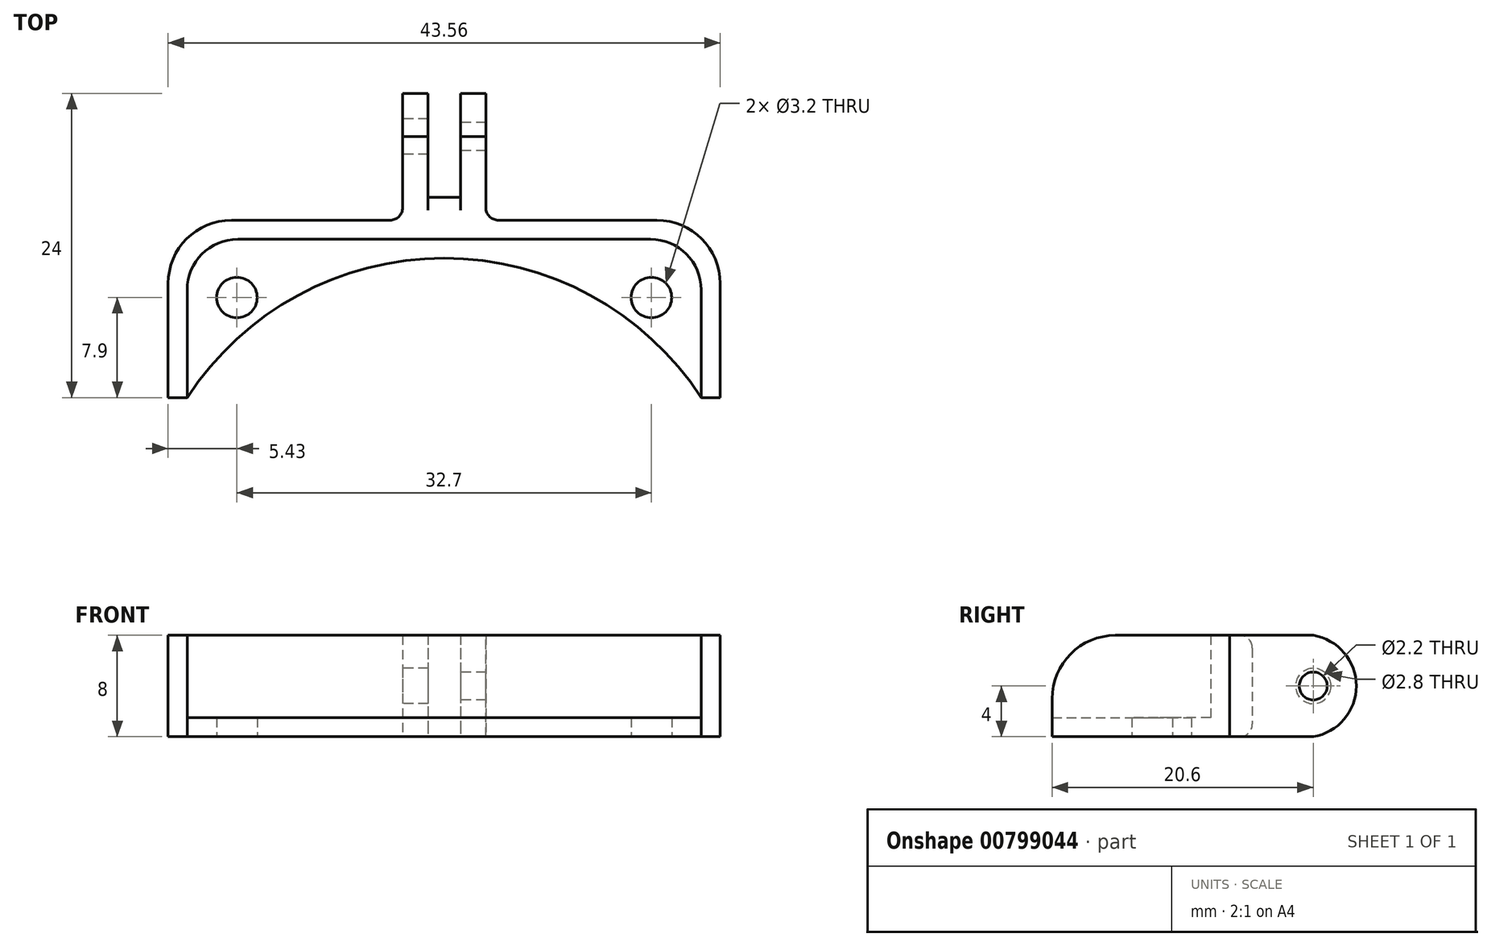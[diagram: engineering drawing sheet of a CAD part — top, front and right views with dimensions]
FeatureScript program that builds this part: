
annotation { "Feature Type Name" : "Feature", "Feature Type Description" : "" }
export const myFeature = defineFeature(function(context is Context, id is Id, definition is map)
    precondition{}
    {
        {
            var Q0;
            Q0=qCreatedBy(makeId("Top.planeOp"),FACE);
            var sketch = newSketch(context, id + "F0", { "sketchPlane" : qUnion([Q0])});
            skLineSegment(sketch, "E0", {"start": v(0, 0) * mm, "end": v(1.28, 0) * mm});
            skLineSegment(sketch, "E1", {"start": v(0, 8.06) * mm, "end": v(0, -20.77) * mm, "construction": true});
            skLineSegment(sketch, "E2", {"start": v(1.28, 0) * mm, "end": v(1.28, 8.2) * mm});
            skLineSegment(sketch, "E3", {"start": v(1.28, 8.2) * mm, "end": v(3.28, 8.2) * mm});
            skLineSegment(sketch, "E4", {"start": v(3.28, 8.2) * mm, "end": v(3.28, -1.8) * mm});
            skLineSegment(sketch, "E5", {"start": v(3.28, -1.8) * mm, "end": v(16.78, -1.8) * mm});
            skLineSegment(sketch, "E6", {"start": v(21.78, -6.8) * mm, "end": v(21.78, -15.8) * mm});
            skLineSegment(sketch, "E7", {"start": v(21.78, -15.8) * mm, "end": v(20.28, -15.8) * mm});
            skLineSegment(sketch, "E8", {"start": v(20.28, -15.8) * mm, "end": v(20.28, -7.3) * mm});
            skLineSegment(sketch, "E9", {"start": v(16.28, -3.3) * mm, "end": v(0, -3.3) * mm});
            skCircle(sketch, "E10", {"center": v(16.35, -7.9) * mm, "radius": 1.6 * mm});
            skPoint(sketch, "E11", {"position": v(0, -4.8) * mm});
            skLineSegment(sketch, "E12.MirrorCS", {"start": v(0, 0) * mm, "end": v(-1.28, 0) * mm});
            skLineSegment(sketch, "E13.MirrorCS", {"start": v(-1.28, 0) * mm, "end": v(-1.28, 8.2) * mm});
            skLineSegment(sketch, "E14.MirrorCS", {"start": v(-1.28, 8.2) * mm, "end": v(-3.28, 8.2) * mm});
            skLineSegment(sketch, "E15.MirrorCS", {"start": v(-3.28, 8.2) * mm, "end": v(-3.28, -1.8) * mm});
            skLineSegment(sketch, "E16.MirrorCS", {"start": v(-3.28, -1.8) * mm, "end": v(-16.78, -1.8) * mm});
            skLineSegment(sketch, "E17.MirrorCS", {"start": v(-21.78, -6.8) * mm, "end": v(-21.78, -15.8) * mm});
            skLineSegment(sketch, "E18.MirrorCS", {"start": v(-21.78, -15.8) * mm, "end": v(-20.28, -15.8) * mm});
            skLineSegment(sketch, "E19.MirrorCS", {"start": v(-20.28, -15.8) * mm, "end": v(-20.28, -7.3) * mm});
            skLineSegment(sketch, "E20.MirrorCS", {"start": v(-16.28, -3.3) * mm, "end": v(0, -3.3) * mm});
            skCircle(sketch, "E21.MirrorC", {"center": v(-16.35, -7.9) * mm, "radius": 1.6 * mm});
            skArc(sketch, "E22", {"start": v(20.28, -15.8) * mm, "mid": v(0, -4.8) * mm, "end": v(-20.28, -15.8) * mm});
            skPoint(sketch, "E23.visualSharp", {"position": v(20.28, -3.3) * mm});
            skArc(sketch, "E23.filletArc", {"start": v(20.28, -7.3) * mm, "mid": v(19.1, -4.47) * mm, "end": v(16.28, -3.3) * mm});
            skPoint(sketch, "E24.visualSharp", {"position": v(-20.28, -3.3) * mm});
            skArc(sketch, "E24.filletArc", {"start": v(-16.28, -3.3) * mm, "mid": v(-19.1, -4.47) * mm, "end": v(-20.28, -7.3) * mm});
            skPoint(sketch, "E25.visualSharp", {"position": v(21.78, -1.8) * mm});
            skArc(sketch, "E25.filletArc", {"start": v(21.78, -6.8) * mm, "mid": v(20.32, -3.26) * mm, "end": v(16.78, -1.8) * mm});
            skPoint(sketch, "E26.visualSharp", {"position": v(-21.78, -1.8) * mm});
            skArc(sketch, "E26.filletArc", {"start": v(-16.78, -1.8) * mm, "mid": v(-20.32, -3.26) * mm, "end": v(-21.78, -6.8) * mm});
            skSolve(sketch);
        }
        {
            var Q0;
            Q0=makeQuery(id+"F0.imprint","IMPRINT",FACE,{"disambiguationData":[TD([[makeQuery(id+"F0.imprint","IMPRINT",EDGE,{"derivedFrom":sQuery(id+"F0.wireOp",EDGE,"E0")}),-1.0]])]});
            extrude(context, id + "F1", {"entities" : qUnion([Q0]), "depth" : 8 * mm, "offsetDistance" : 25 * mm});
        }
        {
            var Q0;
            Q0=makeQuery(id+"F0.imprint","IMPRINT",FACE,{"disambiguationData":[TD([[makeQuery(id+"F0.imprint","IMPRINT",EDGE,{"derivedFrom":sQuery(id+"F0.wireOp",EDGE,"E8")}),1.0]])]});
            extrude(context, id + "F2", {"entities" : qUnion([Q0]), "operationType" : NewBodyOperationType.ADD, "depth" : 1.5 * mm, "offsetDistance" : 25 * mm});
        }
        {
            var Q0;
            Q0=makeQuery(id+"F1.opExtrude","SWEPT_FACE",FACE,{"disambiguationData":[OSD([sQuery(id+"F0.wireOp",EDGE,"E15.MirrorCS")])]});
            var sketch = newSketch(context, id + "F3", { "sketchPlane" : qUnion([Q0])});
            skCircle(sketch, "E27", {"center": v(-4.8, 4) * mm, "radius": 1.1 * mm});
            skPoint(sketch, "E27.centerSnap0", {"position": v(-8.2, 4) * mm});
            skCircle(sketch, "E28", {"center": v(-4.8, 4) * mm, "radius": 1.4 * mm});
            skLineSegment(sketch, "E29", {"start": v(-4.8, -1.3) * mm, "end": v(-4.8, 9.5) * mm, "construction": true});
            skArc(sketch, "E30", {"start": v(-4.8, 8) * mm, "mid": v(-8.2, 4) * mm, "end": v(-4.8, 0) * mm});
            skSolve(sketch);
        }
        {
            var Q0;
            Q0=makeQuery(id+"F3.imprint","IMPRINT",FACE,{"disambiguationData":[TD([[makeQuery(id+"F3.imprint","IMPRINT",EDGE,{"derivedFrom":sQuery(id+"F3.wireOp",EDGE,"E27")}),1.0]])]});
            var Q1;
            {var subQ0=sQuery(id+"F3.wireOp",EDGE,"E30");var subQ1=sQuery(id+"F0.wireOp",EDGE,"E15.MirrorCS");var subQ2=makeQuery(id+"F1.opExtrude","CAP_EDGE",EDGE,{"disambiguationData":[OSD([subQ1])],"isStart":true});var subQ3=makeQuery(id+"F3.imprint","INTERSECT",VERTEX,{"derivedFrom":[subQ2,subQ0]});Q1=makeQuery(id+"F3.imprint","IMPRINT",FACE,{"disambiguationData":[TD([[makeQuery(id+"F3.imprint","IMPRINT",EDGE,{"disambiguationData":[TD([[subQ3,1.0]])],"derivedFrom":subQ0}),-1.0]])]});}
            var Q2;
            {var subQ0=sQuery(id+"F3.wireOp",EDGE,"E30");var subQ1=sQuery(id+"F0.wireOp",EDGE,"E15.MirrorCS");var subQ2=makeQuery(id+"F1.opExtrude","CAP_EDGE",EDGE,{"disambiguationData":[OSD([subQ1])],"isStart":false});var subQ3=makeQuery(id+"F3.imprint","INTERSECT",VERTEX,{"derivedFrom":[subQ2,subQ0]});Q2=makeQuery(id+"F3.imprint","IMPRINT",FACE,{"disambiguationData":[TD([[makeQuery(id+"F3.imprint","IMPRINT",EDGE,{"disambiguationData":[TD([[subQ3,-1.0]])],"derivedFrom":subQ0}),-1.0]])]});}
            extrude(context, id + "F4", {"entities" : qUnion([Q0, Q1, Q2]), "operationType" : NewBodyOperationType.REMOVE, "oppositeDirection" : true, "depth" : 8 * mm, "offsetDistance" : 25 * mm});
        }
        {
            var Q0;
            Q0=makeQuery(id+"F3.imprint","IMPRINT",FACE,{"disambiguationData":[TD([[makeQuery(id+"F3.imprint","IMPRINT",EDGE,{"derivedFrom":sQuery(id+"F3.wireOp",EDGE,"E27")}),-1.0]])]});
            extrude(context, id + "F5", {"entities" : qUnion([Q0]), "operationType" : NewBodyOperationType.REMOVE, "oppositeDirection" : true, "depth" : 2.4 * mm, "offsetDistance" : 25 * mm});
        }
        {
            var Q0;
            Q0=makeQuery(id+"F2.opExtrude","CAP_EDGE",EDGE,{"disambiguationData":[OSD([sQuery(id+"F0.wireOp",EDGE,"E19.MirrorCS")])],"isStart":false});
            var Q1;
            Q1=makeQuery(id+"F1.opExtrude","SWEPT_EDGE",EDGE,{"disambiguationData":[OSD([sQuery(id+"F0.wireOp",EDGE,"E15.MirrorCS"),sQuery(id+"F0.wireOp",EDGE,"E16.MirrorCS")])]});
            var Q2;
            Q2=makeQuery(id+"F1.opExtrude","SWEPT_EDGE",EDGE,{"disambiguationData":[OSD([sQuery(id+"F0.wireOp",EDGE,"E4"),sQuery(id+"F0.wireOp",EDGE,"E5")])]});
            var Q3;
            Q3=makeQuery(id+"F1.opExtrude","CAP_EDGE",EDGE,{"disambiguationData":[OSD([sQuery(id+"F0.wireOp",EDGE,"E0"),sQuery(id+"F0.wireOp",EDGE,"E12.MirrorCS")])],"isStart":false});
            var Q4;
            Q4=makeQuery(id+"F1.opExtrude","CAP_EDGE",EDGE,{"disambiguationData":[OSD([sQuery(id+"F0.wireOp",EDGE,"E0"),sQuery(id+"F0.wireOp",EDGE,"E12.MirrorCS")])],"isStart":true});
            fillet(context, id + "F6", {"entities" : qUnion([Q0, Q1, Q2, Q3, Q4]), "radius" : 1 * mm, "tangentPropagation" : true, "allowEdgeOverflow" : false});
        }
        {
            var Q0;
            Q0=makeQuery(id+"F1.opExtrude","CAP_EDGE",EDGE,{"disambiguationData":[OSD([sQuery(id+"F0.wireOp",EDGE,"E18.MirrorCS")])],"isStart":false});
            var Q1;
            Q1=makeQuery(id+"F1.opExtrude","CAP_EDGE",EDGE,{"disambiguationData":[OSD([sQuery(id+"F0.wireOp",EDGE,"E7")])],"isStart":false});
            fillet(context, id + "F7", {"entities" : qUnion([Q0, Q1]), "radius" : 5 * mm, "tangentPropagation" : true, "allowEdgeOverflow" : false});
        }
    });
